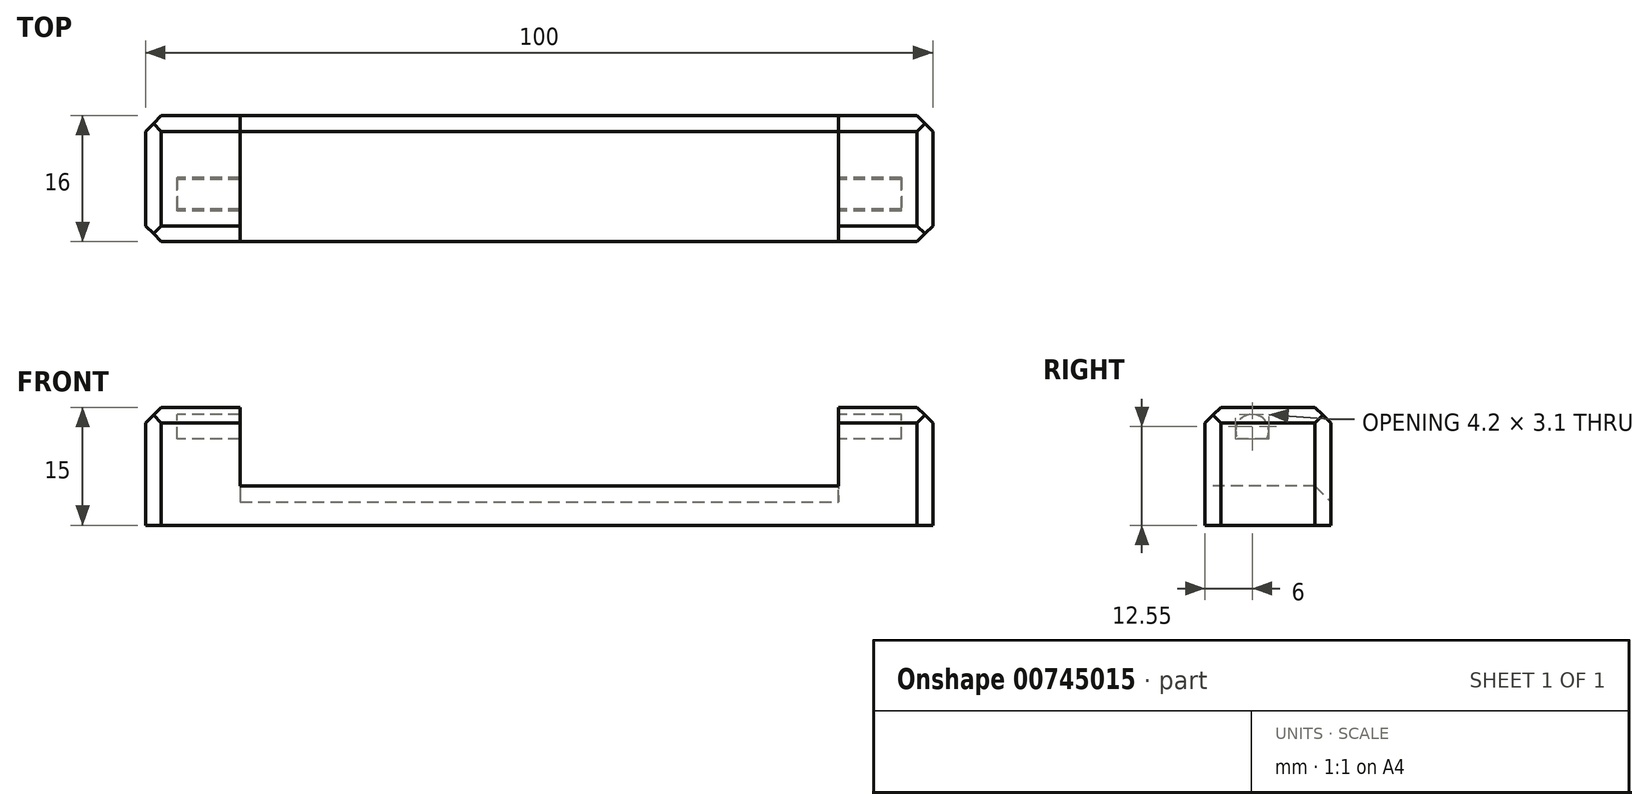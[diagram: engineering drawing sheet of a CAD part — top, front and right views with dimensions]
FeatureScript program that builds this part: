
annotation { "Feature Type Name" : "Feature", "Feature Type Description" : "" }
export const myFeature = defineFeature(function(context is Context, id is Id, definition is map)
    precondition{}
    {
        {
            var Q0;
            Q0=qCreatedBy(makeId("Top.planeOp"),FACE);
            var sketch = newSketch(context, id + "F0", { "sketchPlane" : qUnion([Q0])});
            skLineSegment(sketch, "E0.bottom", {"start": v(50, -8) * mm, "end": v(-50, -8) * mm});
            skLineSegment(sketch, "E0.top", {"start": v(50, 8) * mm, "end": v(-50, 8) * mm});
            skLineSegment(sketch, "E0.left", {"start": v(50, -8) * mm, "end": v(50, 8) * mm});
            skLineSegment(sketch, "E0.right", {"start": v(-50, -8) * mm, "end": v(-50, 8) * mm});
            skPoint(sketch, "E0.middle", {"position": v(0, 0) * mm});
            skSolve(sketch);
        }
        {
            var Q0;
            Q0=makeQuery(id+"F0.imprint","IMPRINT",FACE,{"disambiguationData":[TD([[makeQuery(id+"F0.imprint","IMPRINT",EDGE,{"derivedFrom":sQuery(id+"F0.wireOp",EDGE,"E0.bottom")}),-1.0]])]});
            extrude(context, id + "F1", {"entities" : qUnion([Q0]), "depth" : 3 * mm, "offsetDistance" : 25 * mm});
        }
        {
            var Q0;
            Q0=makeQuery(id+"F1.opExtrude","CAP_FACE",FACE,{"disambiguationData":[OSD([sQuery(id+"F0.wireOp",EDGE,"E0.bottom"),sQuery(id+"F0.wireOp",EDGE,"E0.top"),sQuery(id+"F0.wireOp",EDGE,"E0.left"),sQuery(id+"F0.wireOp",EDGE,"E0.right")])],"isStart":false});
            var sketch = newSketch(context, id + "F2", { "sketchPlane" : qUnion([Q0])});
            skLineSegment(sketch, "E1.bottom", {"start": v(-50, 8) * mm, "end": v(-38, 8) * mm});
            skLineSegment(sketch, "E1.top", {"start": v(-50, -8) * mm, "end": v(-38, -8) * mm});
            skLineSegment(sketch, "E1.left", {"start": v(-50, 8) * mm, "end": v(-50, -8) * mm});
            skLineSegment(sketch, "E1.right", {"start": v(-38, 8) * mm, "end": v(-38, -8) * mm});
            skLineSegment(sketch, "E2.MirrorCS", {"start": v(38, 8) * mm, "end": v(38, -8) * mm});
            skLineSegment(sketch, "E3.MirrorCS", {"start": v(50, 8) * mm, "end": v(38, 8) * mm});
            skLineSegment(sketch, "E4.MirrorCS", {"start": v(50, 8) * mm, "end": v(50, -8) * mm});
            skLineSegment(sketch, "E5.MirrorCS", {"start": v(50, -8) * mm, "end": v(38, -8) * mm});
            skSolve(sketch);
        }
        {
            var Q0;
            Q0=makeQuery(id+"F2.imprint","IMPRINT",FACE,{"disambiguationData":[TD([[makeQuery(id+"F2.imprint","IMPRINT",EDGE,{"derivedFrom":sQuery(id+"F2.wireOp",EDGE,"E1.bottom")}),1.0]])]});
            var Q1;
            Q1=makeQuery(id+"F2.imprint","IMPRINT",FACE,{"disambiguationData":[TD([[makeQuery(id+"F2.imprint","IMPRINT",EDGE,{"derivedFrom":sQuery(id+"F2.wireOp",EDGE,"E2.MirrorCS")}),1.0]])]});
            extrude(context, id + "F3", {"entities" : qUnion([Q0, Q1]), "operationType" : NewBodyOperationType.ADD, "depth" : 10 * mm, "offsetDistance" : 25 * mm});
        }
        {
            var Q0;
            Q0=makeQuery(id+"F3.boolean.opBoolean","MERGE",EDGE,{"derivedFrom":[makeQuery(id+"F1.opExtrude","SWEPT_EDGE",EDGE,{"disambiguationData":[OSD([sQuery(id+"F0.wireOp",EDGE,"E0.top"),sQuery(id+"F0.wireOp",EDGE,"E0.right")])]}),makeQuery(id+"F3.opExtrude","SWEPT_EDGE",EDGE,{"disambiguationData":[OSD([sQuery(id+"F2.wireOp",EDGE,"E1.bottom"),sQuery(id+"F2.wireOp",EDGE,"E1.left")])]})]});
            var Q1;
            Q1=makeQuery(id+"F3.opExtrude","CAP_EDGE",EDGE,{"disambiguationData":[OSD([sQuery(id+"F2.wireOp",EDGE,"E1.left")])],"isStart":false});
            var Q2;
            Q2=makeQuery(id+"F3.boolean.opBoolean","MERGE",EDGE,{"derivedFrom":[makeQuery(id+"F1.opExtrude","SWEPT_EDGE",EDGE,{"disambiguationData":[OSD([sQuery(id+"F0.wireOp",EDGE,"E0.bottom"),sQuery(id+"F0.wireOp",EDGE,"E0.right")])]}),makeQuery(id+"F3.opExtrude","SWEPT_EDGE",EDGE,{"disambiguationData":[OSD([sQuery(id+"F2.wireOp",EDGE,"E1.top"),sQuery(id+"F2.wireOp",EDGE,"E1.left")])]})]});
            var Q3;
            Q3=makeQuery(id+"F3.boolean.opBoolean","MERGE",EDGE,{"derivedFrom":[makeQuery(id+"F1.opExtrude","SWEPT_EDGE",EDGE,{"disambiguationData":[OSD([sQuery(id+"F0.wireOp",EDGE,"E0.bottom"),sQuery(id+"F0.wireOp",EDGE,"E0.left")])]}),makeQuery(id+"F3.opExtrude","SWEPT_EDGE",EDGE,{"disambiguationData":[OSD([sQuery(id+"F2.wireOp",EDGE,"E4.MirrorCS"),sQuery(id+"F2.wireOp",EDGE,"E5.MirrorCS")])]})]});
            var Q4;
            Q4=makeQuery(id+"F3.opExtrude","CAP_EDGE",EDGE,{"disambiguationData":[OSD([sQuery(id+"F2.wireOp",EDGE,"E4.MirrorCS")])],"isStart":false});
            var Q5;
            Q5=makeQuery(id+"F3.boolean.opBoolean","MERGE",EDGE,{"derivedFrom":[makeQuery(id+"F1.opExtrude","SWEPT_EDGE",EDGE,{"disambiguationData":[OSD([sQuery(id+"F0.wireOp",EDGE,"E0.top"),sQuery(id+"F0.wireOp",EDGE,"E0.left")])]}),makeQuery(id+"F3.opExtrude","SWEPT_EDGE",EDGE,{"disambiguationData":[OSD([sQuery(id+"F2.wireOp",EDGE,"E3.MirrorCS"),sQuery(id+"F2.wireOp",EDGE,"E4.MirrorCS")])]})]});
            chamfer(context, id + "F4", {"entities" : qUnion([Q0, Q1, Q2, Q3, Q4, Q5]), "width" : 2 * mm, "tangentPropagation" : true});
        }
        {
            var Q0;
            Q0=makeQuery(id+"F3.opExtrude","CAP_EDGE",EDGE,{"disambiguationData":[OSD([sQuery(id+"F2.wireOp",EDGE,"E1.top")])],"isStart":false});
            var Q1;
            Q1=makeQuery(id+"F3.opExtrude","CAP_EDGE",EDGE,{"disambiguationData":[OSD([sQuery(id+"F2.wireOp",EDGE,"E1.bottom")])],"isStart":false});
            var Q2;
            Q2=makeQuery(id+"F3.opExtrude","CAP_EDGE",EDGE,{"disambiguationData":[OSD([sQuery(id+"F2.wireOp",EDGE,"E3.MirrorCS")])],"isStart":false});
            var Q3;
            Q3=makeQuery(id+"F3.opExtrude","CAP_EDGE",EDGE,{"disambiguationData":[OSD([sQuery(id+"F2.wireOp",EDGE,"E5.MirrorCS")])],"isStart":false});
            chamfer(context, id + "F5", {"entities" : qUnion([Q0, Q1, Q2, Q3]), "width" : 2 * mm, "tangentPropagation" : true});
        }
        {
            var Q0;
            Q0=makeQuery(id+"F1.opExtrude","CAP_EDGE",EDGE,{"disambiguationData":[OSD([sQuery(id+"F0.wireOp",EDGE,"E0.top")])],"isStart":false});
            chamfer(context, id + "F6", {"entities" : qUnion([Q0]), "width" : 2 * mm, "tangentPropagation" : true});
        }
        {
            var Q0;
            Q0=makeQuery(id+"F3.opExtrude","SWEPT_FACE",FACE,{"disambiguationData":[OSD([sQuery(id+"F2.wireOp",EDGE,"E1.right")])]});
            var sketch = newSketch(context, id + "F7", { "sketchPlane" : qUnion([Q0])});
            skArc(sketch, "E6", {"start": v(-0.15, 9) * mm, "mid": v(-2, 12.1) * mm, "end": v(-3.85, 9) * mm});
            skLineSegment(sketch, "E7", {"start": v(-3.85, 9) * mm, "end": v(-0.15, 9) * mm});
            skSolve(sketch);
        }
        {
            var Q0;
            Q0=makeQuery(id+"F7.imprint","IMPRINT",FACE,{"disambiguationData":[TD([[makeQuery(id+"F7.imprint","IMPRINT",EDGE,{"derivedFrom":sQuery(id+"F7.wireOp",EDGE,"E6")}),1.0]])]});
            extrude(context, id + "F8", {"entities" : qUnion([Q0]), "depth" : 84 * mm, "offsetDistance" : 25 * mm, "hasSecondDirection" : true, "secondDirectionOppositeDirection" : true, "secondDirectionDepth" : 8 * mm});
        }
        {
            var Q0;
            Q0=makeQuery(id+"F1.opExtrude","CAP_FACE",FACE,{"disambiguationData":[OSD([sQuery(id+"F0.wireOp",EDGE,"E0.bottom"),sQuery(id+"F0.wireOp",EDGE,"E0.top"),sQuery(id+"F0.wireOp",EDGE,"E0.left"),sQuery(id+"F0.wireOp",EDGE,"E0.right")])],"isStart":true});
            extrude(context, id + "F9", {"entities" : qUnion([Q0]), "operationType" : NewBodyOperationType.ADD, "depth" : 2 * mm, "offsetDistance" : 25 * mm});
        }
        {
            var Q0;
            Q0=makeQuery(id+"F8.opExtrude","SWEPT_BODY",BODY,{"disambiguationData":[OSD([sQuery(id+"F7.wireOp",EDGE,"E6"),sQuery(id+"F7.wireOp",EDGE,"E7")])]});
            var Q1;
            Q1=makeQuery(id+"F1.opExtrude","SWEPT_BODY",BODY,{"disambiguationData":[OSD([sQuery(id+"F0.wireOp",EDGE,"E0.bottom"),sQuery(id+"F0.wireOp",EDGE,"E0.top"),sQuery(id+"F0.wireOp",EDGE,"E0.left"),sQuery(id+"F0.wireOp",EDGE,"E0.right")])]});
            booleanBodies(context, id + "F10", {"operationType" : BooleanOperationType.SUBTRACTION, "tools" : qUnion([Q0]), "targets" : qUnion([Q1])});
        }
    });
